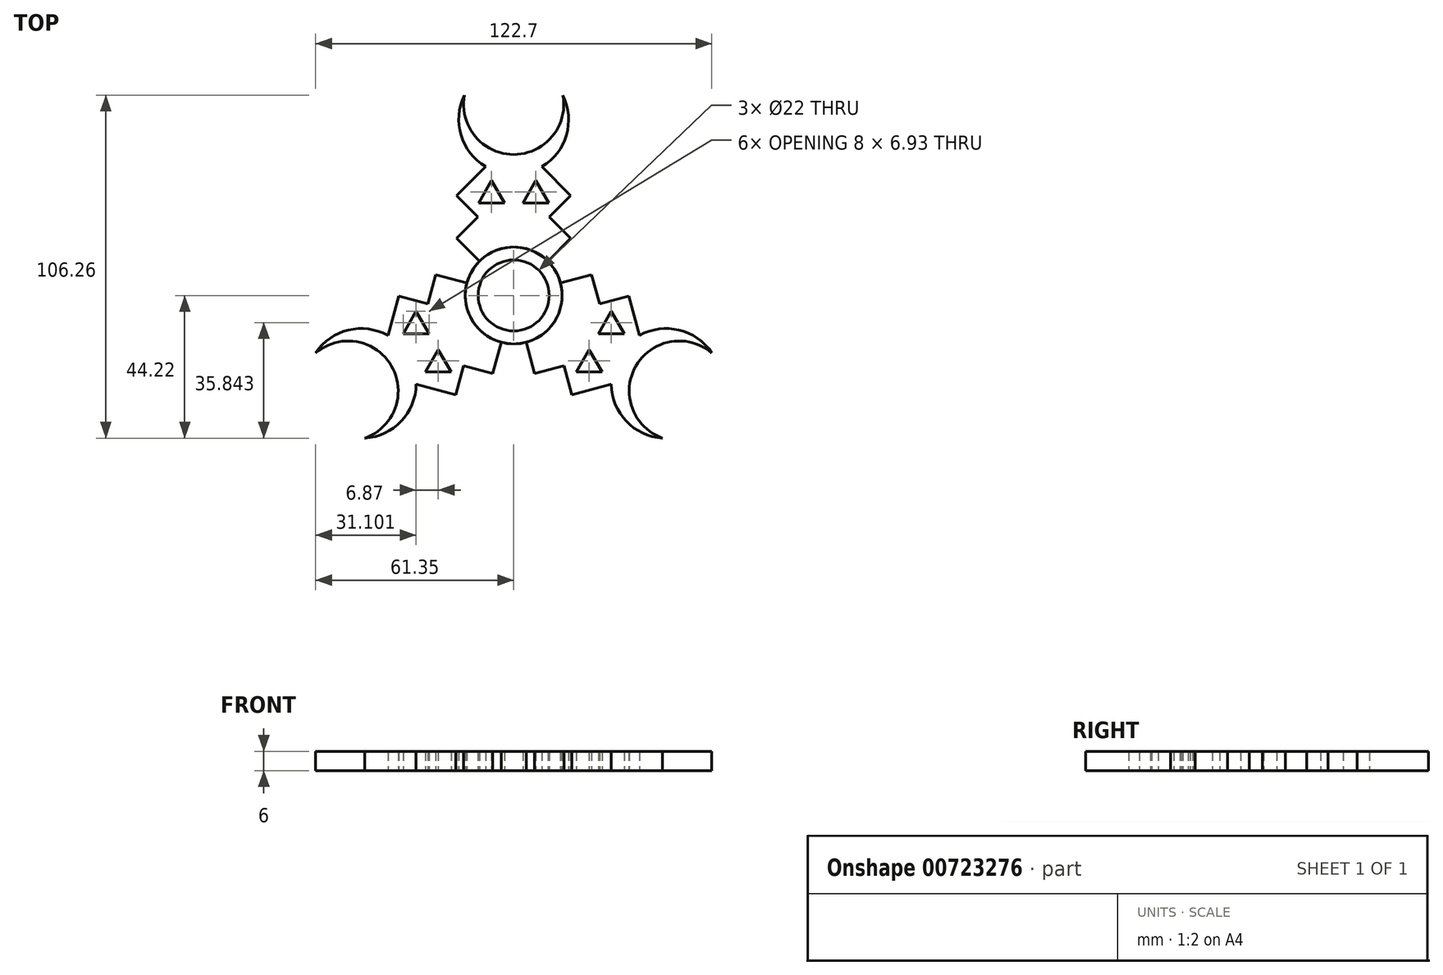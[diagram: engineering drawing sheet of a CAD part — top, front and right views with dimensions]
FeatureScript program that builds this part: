
annotation { "Feature Type Name" : "Feature", "Feature Type Description" : "" }
export const myFeature = defineFeature(function(context is Context, id is Id, definition is map)
    precondition{}
    {
        {
            var Q0;
            Q0=qCreatedBy(makeId("Top.planeOp"),FACE);
            var sketch = newSketch(context, id + "F0", { "sketchPlane" : qUnion([Q0])});
            skCircle(sketch, "E0", {"center": v(0, 0) * mm, "radius": 11 * mm});
            skCircle(sketch, "E1", {"center": v(0, 0) * mm, "radius": 15 * mm});
            skLineSegment(sketch, "E2.bottom", {"start": v(-17.68, 17.68) * mm, "end": v(-11.04, 24.32) * mm});
            skLineSegment(sketch, "E2.top", {"start": v(10.6, 10.6) * mm, "end": v(17.68, 17.68) * mm});
            skLineSegment(sketch, "E2.left", {"start": v(-17.68, 17.68) * mm, "end": v(-10.6, 10.6) * mm});
            skLineSegment(sketch, "E2.right", {"start": v(11.04, 24.32) * mm, "end": v(17.68, 17.68) * mm});
            skLineSegment(sketch, "E3.bottom", {"start": v(-17.68, 30.96) * mm, "end": v(-8.73, 39.91) * mm});
            skLineSegment(sketch, "E3.top", {"start": v(1.63, 14.91) * mm, "end": v(17.68, 30.96) * mm});
            skLineSegment(sketch, "E3.left", {"start": v(-17.68, 30.96) * mm, "end": v(-1.63, 14.91) * mm});
            skLineSegment(sketch, "E3.right", {"start": v(8.73, 39.91) * mm, "end": v(17.68, 30.96) * mm});
            skArc(sketch, "E4", {"start": v(-15.24, 62.04) * mm, "mid": v(0, 37.5) * mm, "end": v(15.24, 62.04) * mm});
            skArc(sketch, "E5", {"start": v(-15.24, 62.04) * mm, "mid": v(0, 43.7) * mm, "end": v(15.24, 62.04) * mm});
            skLineSegment(sketch, "E6.0", {"start": v(-6.87, 35.58) * mm, "end": v(-2.87, 28.65) * mm});
            skLineSegment(sketch, "E6.1", {"start": v(-2.87, 28.65) * mm, "end": v(-10.87, 28.65) * mm});
            skLineSegment(sketch, "E6.2", {"start": v(-10.87, 28.65) * mm, "end": v(-6.87, 35.58) * mm});
            skPoint(sketch, "E6.0.midPoint", {"position": v(-4.87, 32.12) * mm});
            skLineSegment(sketch, "E7", {"start": v(-17.68, 30.96) * mm, "end": v(1.92, 30.96) * mm, "construction": true});
            skLineSegment(sketch, "E8.MirrorCS", {"start": v(10.87, 28.65) * mm, "end": v(6.87, 35.58) * mm});
            skLineSegment(sketch, "E9.MirrorCS", {"start": v(6.87, 35.58) * mm, "end": v(2.87, 28.65) * mm});
            skLineSegment(sketch, "E10.MirrorCS", {"start": v(2.87, 28.65) * mm, "end": v(10.87, 28.65) * mm});
            skLineSegment(sketch, "E11.MirrorCS", {"start": v(17.68, 30.96) * mm, "end": v(-1.92, 30.96) * mm, "construction": true});
            skPoint(sketch, "E12.MirrorP", {"position": v(4.87, 32.12) * mm});
            skSolve(sketch);
        }
        {
            var Q0;
            Q0 = qSketchRegion(id + "F0", true);
            extrude(context, id + "F1", {"entities" : qUnion([Q0]), "depth" : 6 * mm, "offsetDistance" : 25 * mm});
        }
        {
            var Q0;
            Q0=makeQuery(id+"F1.opExtrude","SWEPT_BODY",BODY,{"disambiguationData":[OSD([sQuery(id+"F0.wireOp",EDGE,"E0"),sQuery(id+"F0.wireOp",EDGE,"E1"),sQuery(id+"F0.wireOp",EDGE,"E2.bottom"),sQuery(id+"F0.wireOp",EDGE,"E2.top"),sQuery(id+"F0.wireOp",EDGE,"E2.left"),sQuery(id+"F0.wireOp",EDGE,"E2.right"),sQuery(id+"F0.wireOp",EDGE,"E3.bottom"),sQuery(id+"F0.wireOp",EDGE,"E3.top"),sQuery(id+"F0.wireOp",EDGE,"E3.left"),sQuery(id+"F0.wireOp",EDGE,"E3.right"),sQuery(id+"F0.wireOp",EDGE,"E4"),sQuery(id+"F0.wireOp",EDGE,"E5"),sQuery(id+"F0.wireOp",EDGE,"E6.0"),sQuery(id+"F0.wireOp",EDGE,"E6.1"),sQuery(id+"F0.wireOp",EDGE,"E6.2"),sQuery(id+"F0.wireOp",EDGE,"E8.MirrorCS"),sQuery(id+"F0.wireOp",EDGE,"E9.MirrorCS"),sQuery(id+"F0.wireOp",EDGE,"E10.MirrorCS")])]});
            var Q1;
            Q1=makeQuery(id+"F1.opExtrude","CAP_EDGE",EDGE,{"disambiguationData":[OSD([sQuery(id+"F0.wireOp",EDGE,"E0")])],"isStart":false});
            circularPattern(context, id + "F2", {"entities" : qUnion([Q0]), "axis" : qUnion([Q1]), "angle" : 360 * degree, "instanceCount" : 3, "equalSpace" : true});
        }
    });
